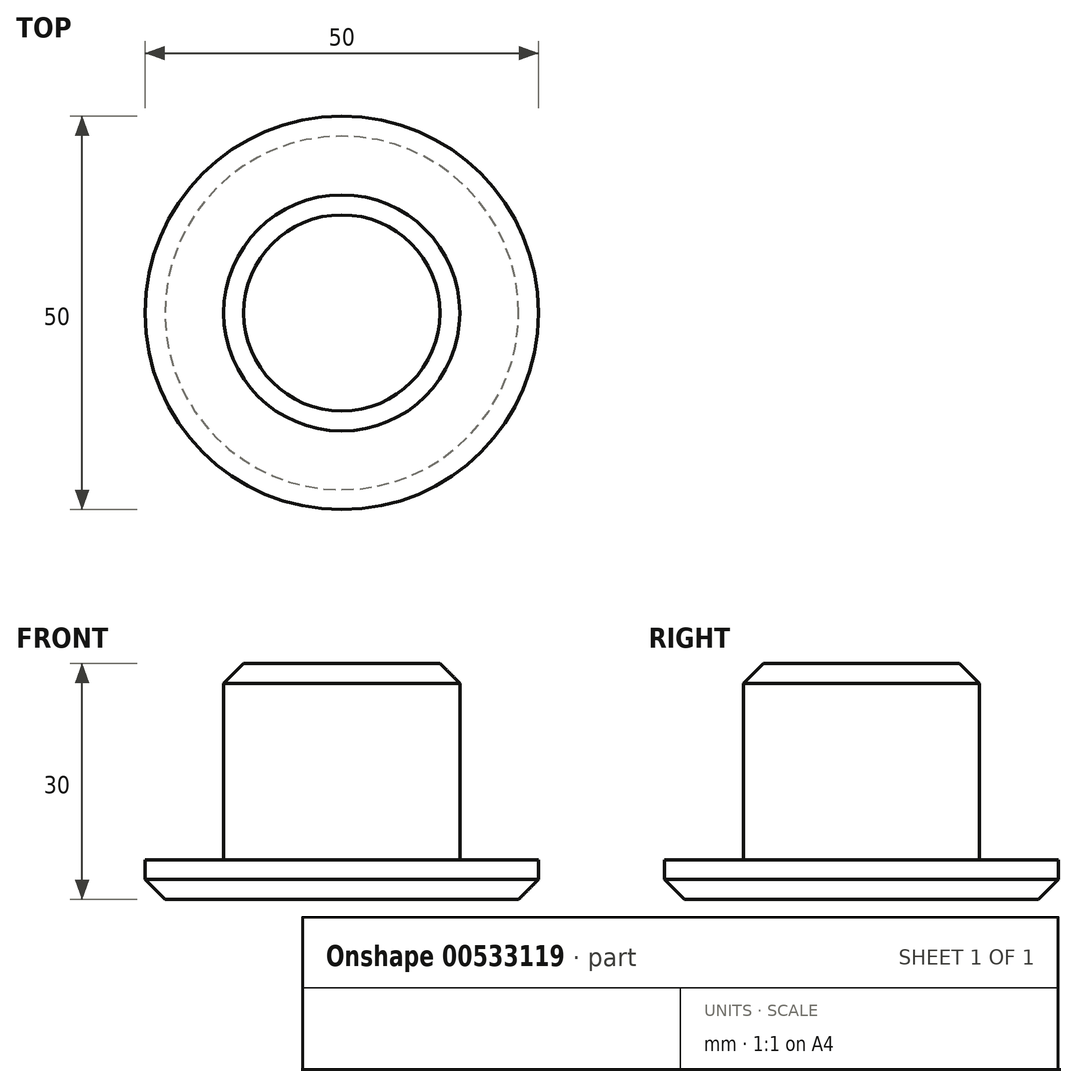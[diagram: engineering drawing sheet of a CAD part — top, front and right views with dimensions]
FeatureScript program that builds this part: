
annotation { "Feature Type Name" : "Feature", "Feature Type Description" : "" }
export const myFeature = defineFeature(function(context is Context, id is Id, definition is map)
    precondition{}
    {
        {
            var Q0;
            Q0=qCreatedBy(makeId("Top.planeOp"),FACE);
            var sketch = newSketch(context, id + "F0", { "sketchPlane" : qUnion([Q0])});
            skCircle(sketch, "E0", {"center": v(0, 0) * mm, "radius": 15 * mm});
            skCircle(sketch, "E1", {"center": v(0, 0) * mm, "radius": 25 * mm});
            skSolve(sketch);
        }
        {
            var Q0;
            Q0=makeQuery(id+"F0.imprint","IMPRINT",FACE,{"disambiguationData":[TD([[makeQuery(id+"F0.imprint","IMPRINT",EDGE,{"derivedFrom":sQuery(id+"F0.wireOp",EDGE,"E0")}),1.0]])]});
            extrude(context, id + "F1", {"entities" : qUnion([Q0]), "depth" : 25 * mm, "offsetDistance" : 25.4 * mm});
        }
        {
            var Q0;
            Q0=makeQuery(id+"F0.imprint","IMPRINT",FACE,{"disambiguationData":[TD([[makeQuery(id+"F0.imprint","IMPRINT",EDGE,{"derivedFrom":sQuery(id+"F0.wireOp",EDGE,"E0")}),-1.0]])]});
            var Q1;
            Q1=makeQuery(id+"F1.opExtrude","CAP_FACE",FACE,{"disambiguationData":[OSD([sQuery(id+"F0.wireOp",EDGE,"E0")])],"isStart":false});
            extrude(context, id + "F2", {"entities" : qUnion([Q0, Q1]), "operationType" : NewBodyOperationType.ADD, "depth" : 5 * mm, "offsetDistance" : 25.4 * mm});
        }
        {
            var Q0;
            Q0=makeQuery(id+"F2.opExtrude","CAP_EDGE",EDGE,{"disambiguationData":[OSD([sQuery(id+"F0.wireOp",EDGE,"E1")])],"isStart":true});
            chamfer(context, id + "F3", {"entities" : qUnion([Q0]), "width" : 2.54 * mm, "tangentPropagation" : true});
        }
        {
            var Q0;
            {var subQ0=sQuery(id+"F0.wireOp",EDGE,"E0");Q0=makeQuery(id+"F2.opExtrude","CAP_EDGE",EDGE,{"disambiguationData":[OSD([subQ0]),TDD([makeQuery(id+"F1.opExtrude","CAP_EDGE",EDGE,{"disambiguationData":[OSD([subQ0])],"isStart":false})])],"isStart":false});}
            chamfer(context, id + "F4", {"entities" : qUnion([Q0]), "width" : 2.54 * mm, "tangentPropagation" : true});
        }
    });
